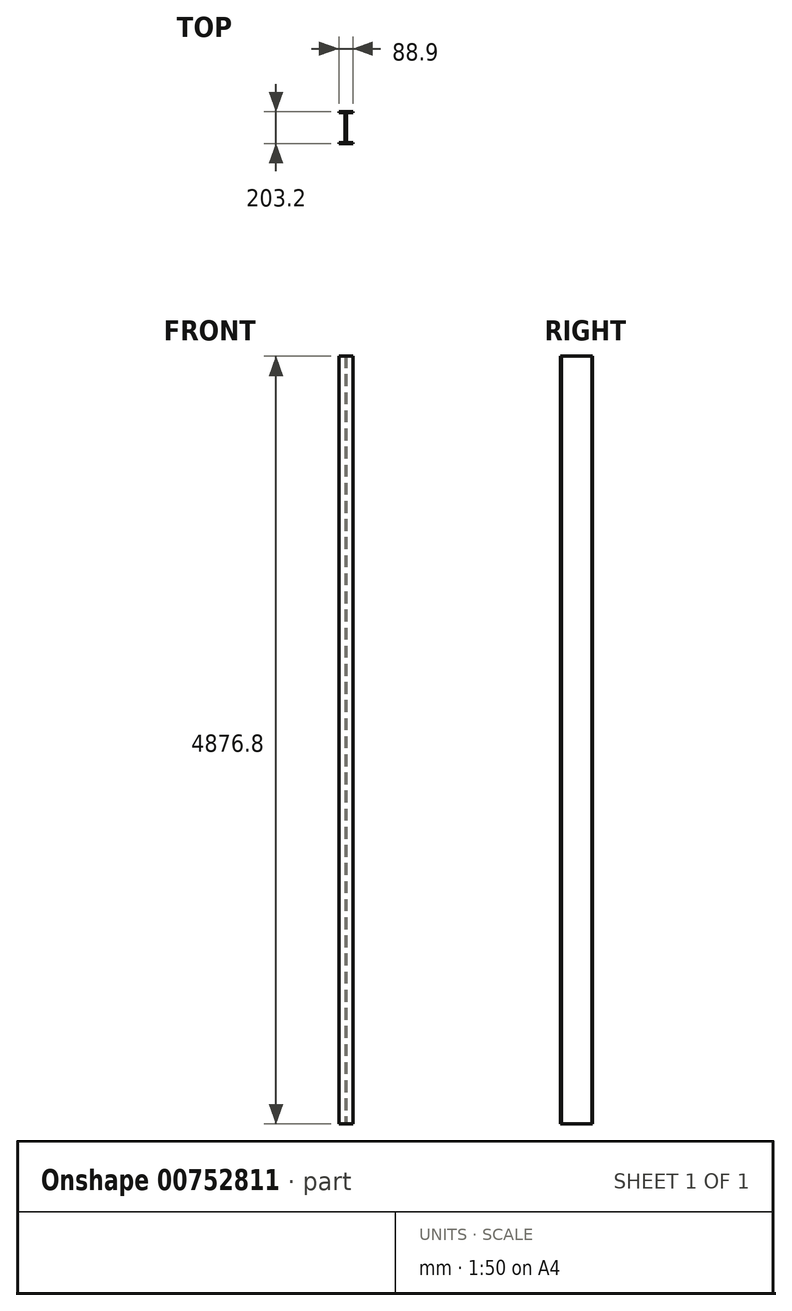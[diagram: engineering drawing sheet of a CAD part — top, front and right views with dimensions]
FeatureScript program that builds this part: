
annotation { "Feature Type Name" : "Feature", "Feature Type Description" : "" }
export const myFeature = defineFeature(function(context is Context, id is Id, definition is map)
    precondition{}
    {
        {
            var Q0;
            Q0=qCreatedBy(makeId("Top.planeOp"),FACE);
            var sketch = newSketch(context, id + "F0", { "sketchPlane" : qUnion([Q0])});
            skLineSegment(sketch, "E0.bottom", {"start": v(44.45, 101.6) * mm, "end": v(-44.45, 101.6) * mm});
            skLineSegment(sketch, "E0.top", {"start": v(44.45, -101.6) * mm, "end": v(-44.45, -101.6) * mm});
            skLineSegment(sketch, "E0.left", {"start": v(44.45, 101.6) * mm, "end": v(44.45, -101.6) * mm});
            skLineSegment(sketch, "E0.right", {"start": v(-44.45, 101.6) * mm, "end": v(-44.45, -101.6) * mm});
            skPoint(sketch, "E0.middle", {"position": v(0, 0) * mm});
            skSolve(sketch);
        }
        {
            var Q0;
            Q0=makeQuery(id+"F0.imprint","IMPRINT",FACE,{"disambiguationData":[TD([[makeQuery(id+"F0.imprint","IMPRINT",EDGE,{"derivedFrom":sQuery(id+"F0.wireOp",EDGE,"E0.bottom")}),1.0]])]});
            extrude(context, id + "F1", {"entities" : qUnion([Q0]), "depth" : 4876.8 * mm, "offsetDistance" : 25.4 * mm});
        }
        {
            var Q0;
            Q0=qCreatedBy(makeId("Top.planeOp"),FACE);
            var sketch = newSketch(context, id + "F2", { "sketchPlane" : qUnion([Q0])});
            skLineSegment(sketch, "E1.0.0", {"start": v(44.45, -101.6) * mm, "end": v(-44.45, -101.6) * mm, "construction": true});
            skLineSegment(sketch, "E1.0.1", {"start": v(-44.45, -101.6) * mm, "end": v(-44.45, 101.6) * mm, "construction": true});
            skLineSegment(sketch, "E1.0.2", {"start": v(-44.45, 101.6) * mm, "end": v(44.45, 101.6) * mm, "construction": true});
            skLineSegment(sketch, "E1.0.3", {"start": v(44.45, 101.6) * mm, "end": v(44.45, -101.6) * mm, "construction": true});
            skLineSegment(sketch, "E2.bottom", {"start": v(-44.45, -96.52) * mm, "end": v(-4.76, -96.52) * mm});
            skLineSegment(sketch, "E2.top", {"start": v(-44.45, 96.52) * mm, "end": v(-4.76, 96.52) * mm});
            skLineSegment(sketch, "E2.left", {"start": v(-44.45, -96.52) * mm, "end": v(-44.45, 96.52) * mm});
            skLineSegment(sketch, "E2.right", {"start": v(-4.76, -96.52) * mm, "end": v(-4.76, 96.52) * mm});
            skLineSegment(sketch, "E3.bottom", {"start": v(44.45, -96.52) * mm, "end": v(4.76, -96.52) * mm});
            skLineSegment(sketch, "E3.top", {"start": v(44.45, 96.52) * mm, "end": v(4.76, 96.52) * mm});
            skLineSegment(sketch, "E3.left", {"start": v(44.45, -96.52) * mm, "end": v(44.45, 96.52) * mm});
            skLineSegment(sketch, "E3.right", {"start": v(4.76, -96.52) * mm, "end": v(4.76, 96.52) * mm});
            skSolve(sketch);
        }
        {
            var Q0;
            Q0=makeQuery(id+"F2.imprint","IMPRINT",FACE,{"disambiguationData":[TD([[makeQuery(id+"F2.imprint","IMPRINT",EDGE,{"derivedFrom":sQuery(id+"F2.wireOp",EDGE,"E2.bottom")}),1.0]])]});
            var Q1;
            Q1=makeQuery(id+"F2.imprint","IMPRINT",FACE,{"disambiguationData":[TD([[makeQuery(id+"F2.imprint","IMPRINT",EDGE,{"derivedFrom":sQuery(id+"F2.wireOp",EDGE,"E3.bottom")}),-1.0]])]});
            extrude(context, id + "F3", {"entities" : qUnion([Q0, Q1]), "operationType" : NewBodyOperationType.REMOVE, "endBound" : BoundingType.THROUGH_ALL, "depth" : 25.4 * mm, "offsetDistance" : 25.4 * mm});
        }
    });
